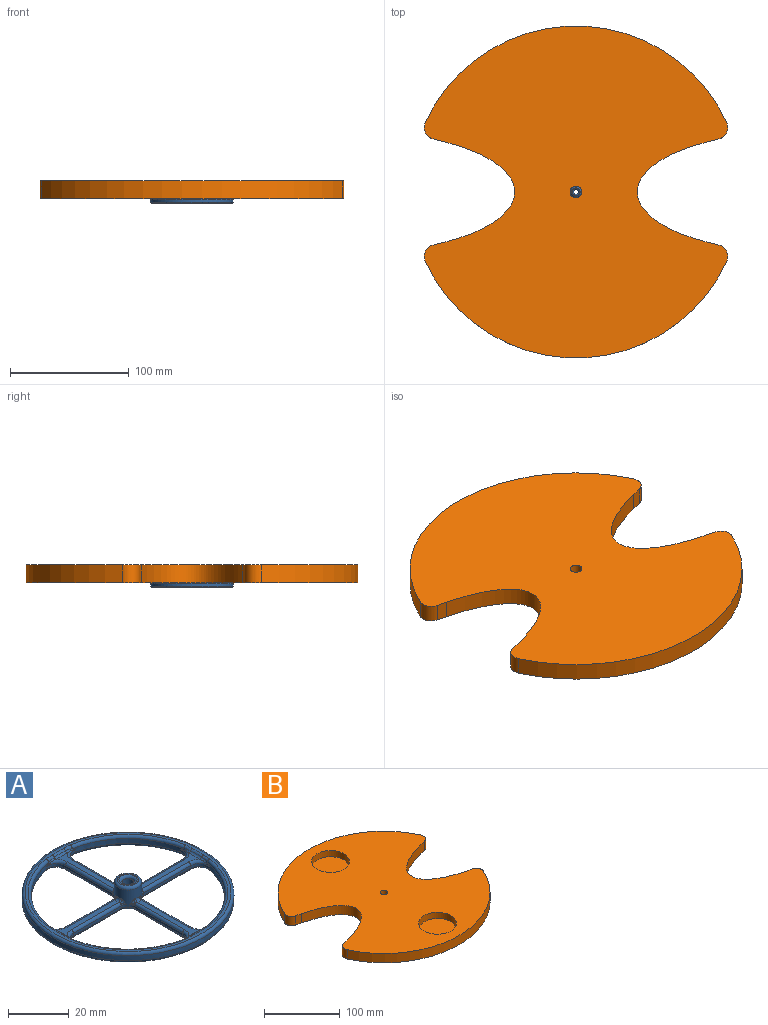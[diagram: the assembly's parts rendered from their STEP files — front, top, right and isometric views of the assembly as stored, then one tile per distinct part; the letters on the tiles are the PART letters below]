
ASSEMBLY  parts=2 mates=1
PART A: 147 faces, bbox 75.8x75.8x9 mm
  f0: cylinder r=32mm len=26.05mm, axis (0,0,1), area 74.3mm2, adj f24,f25,f54,f70,f98,f127
  f1: cylinder r=32mm len=26.05mm, axis (0,0,1), area 74.3mm2, adj f28,f29,f46,f59,f97,f111
  f2: cylinder r=32mm len=26.05mm, axis (0,0,1), area 74.3mm2, adj f26,f27,f74,f87,f106,f119
  f3: plane 68x68mm, normal (0,0,-1), area 521mm2, adj f110,f111,f112,f113,f114,f115,f116,f117
  f4: plane 68x68mm, normal (0,0,1), area 219.2mm2, adj f94,f95,f96,f97,f98,f99,f100,f101
  f5: cylinder r=2mm len=7mm, axis (0,0,-1), area 88mm2, adj f142,f146
  f6: cylinder r=35mm len=70mm, axis (0,0,-1), area 439.8mm2, adj f143,f144
  f7: cylinder r=4.5mm len=9mm, axis (0,0,-1), area 138.5mm2, adj f30,f31,f32,f33,f34,f35,f36,f37
  f8: plane 7x7mm, normal (0,0,1), area 10.2mm2, adj f145,f146
  f9: plane 22.23x1mm, normal (0,-1,0), area 22.2mm2, adj f29,f36,f63,f112
  f10: plane 22.23x1mm, normal (-1,0,0), area 22.2mm2, adj f28,f37,f50,f115
  f11: plane 22.23x1mm, normal (0,1,0), area 22.2mm2, adj f26,f34,f91,f120
  f12: plane 22.23x1mm, normal (1,0,0), area 22.2mm2, adj f27,f35,f78,f123
  f13: plane 22.23x1mm, normal (0,1,0), area 22.2mm2, adj f24,f33,f55,f131
  f14: plane 22.23x1mm, normal (-1,0,0), area 22.2mm2, adj f25,f32,f69,f128
  f15: plane 22.23x1mm, normal (0,-1,0), area 22.2mm2, adj f22,f31,f83,f139
  f16: plane 22.23x1mm, normal (1,0,0), area 22.2mm2, adj f23,f30,f41,f136
  f17: cylinder r=32mm len=26.05mm, axis (0,0,1), area 74.3mm2, adj f22,f23,f42,f82,f105,f135
  f18: plane 25.59x4.96mm, normal (0,0,1), area 54.5mm2, adj f39,f41,f44,f45,f48,f50
  f19: plane 25.59x4.96mm, normal (0,0,1), area 54.5mm2, adj f80,f83,f85,f88,f89,f91
  f20: plane 25.59x4.96mm, normal (0,0,1), area 54.5mm2, adj f67,f69,f72,f73,f76,f78
  f21: plane 25.59x4.96mm, normal (0,0,1), area 54.5mm2, adj f52,f55,f57,f60,f61,f63
  f22: cylinder r=4mm len=4.86mm, axis (0,0,1), area 7.1mm2, adj f15,f17,f80,f137
  f23: cylinder r=4mm len=4.86mm, axis (0,0,1), area 7.1mm2, adj f16,f17,f39,f134
  f24: cylinder r=4mm len=4.86mm, axis (0,0,1), area 7.1mm2, adj f0,f13,f52,f129
  f25: cylinder r=4mm len=4.86mm, axis (0,0,1), area 7.1mm2, adj f0,f14,f67,f126
  f26: cylinder r=4mm len=4.86mm, axis (0,0,1), area 7.1mm2, adj f2,f11,f89,f118
  f27: cylinder r=4mm len=4.86mm, axis (0,0,1), area 7.1mm2, adj f2,f12,f76,f121
  f28: cylinder r=4mm len=4.86mm, axis (0,0,1), area 7.1mm2, adj f1,f10,f48,f113
  f29: cylinder r=4mm len=4.86mm, axis (0,0,1), area 7.1mm2, adj f1,f9,f61,f110
  f30: cylinder r=2mm len=1.58mm, axis (0,0,-1), area 1.8mm2, adj f7,f16,f38,f138
  f31: cylinder r=2mm len=1.58mm, axis (0,0,-1), area 1.8mm2, adj f7,f15,f81,f141
  f32: cylinder r=2mm len=1.58mm, axis (0,0,-1), area 1.8mm2, adj f7,f14,f66,f130
  f33: cylinder r=2mm len=1.58mm, axis (0,0,-1), area 1.8mm2, adj f7,f13,f53,f133
  f34: cylinder r=2mm len=1.58mm, axis (0,0,-1), area 1.8mm2, adj f7,f11,f93,f122
  f35: cylinder r=2mm len=1.58mm, axis (0,0,-1), area 1.8mm2, adj f7,f12,f79,f125
  f36: cylinder r=2mm len=1.58mm, axis (0,0,-1), area 1.8mm2, adj f7,f9,f65,f114
  f37: cylinder r=2mm len=1.58mm, axis (0,0,-1), area 1.8mm2, adj f7,f10,f51,f117
  f38: torus R=3mm, axis (0,0,1), area 1mm2, adj f30,f40,f41
  f39: torus R=5mm, axis (0,0,1), area 8.7mm2, adj f18,f23,f41,f42
  f40: bspline ~1.86x1.69mm, area 1mm2, adj f7,f38,f43
  f41: cylinder r=1mm len=22.23mm, axis (0,1,0), area 34.8mm2, adj f16,f18,f38,f39,f43
  f42: bspline ~4.38x2mm, area 2.9mm2, adj f17,f39,f44,f103
  f43: bspline ~1.47x1.41mm, area 1mm2, adj f7,f40,f41,f45
  f44: torus R=31mm, axis (0,0,1), area 5.3mm2, adj f18,f42,f46,f101
  f45: torus R=5.5mm, axis (0,0,1), area 2.8mm2, adj f7,f18,f43,f47
  f46: bspline ~4.38x2mm, area 2.9mm2, adj f1,f44,f48,f99
  f47: bspline ~1.47x1.41mm, area 1mm2, adj f7,f45,f49,f50
  f48: torus R=5mm, axis (0,0,1), area 8.7mm2, adj f18,f28,f46,f50
  f49: bspline ~1.88x1.71mm, area 1mm2, adj f7,f47,f51
  f50: cylinder r=1mm len=22.23mm, axis (0,-1,0), area 34.8mm2, adj f10,f18,f47,f48,f51
  f51: torus R=3mm, axis (0,0,1), area 1mm2, adj f37,f49,f50
  f52: torus R=5mm, axis (0,0,1), area 8.7mm2, adj f21,f24,f54,f55
  f53: torus R=3mm, axis (0,0,1), area 1mm2, adj f33,f55,f56
  f54: bspline ~4.5x2mm, area 2.9mm2, adj f0,f52,f57,f96
  f55: cylinder r=1mm len=22.23mm, axis (-1,0,0), area 34.8mm2, adj f13,f21,f52,f53,f58
  f56: bspline ~1.88x1.71mm, area 1mm2, adj f7,f53,f58
  f57: torus R=31mm, axis (0,0,1), area 5.3mm2, adj f21,f54,f59,f94
  f58: bspline ~1.47x1.41mm, area 1mm2, adj f7,f55,f56,f60
  f59: bspline ~4.99x2mm, area 2.9mm2, adj f1,f57,f61,f95
  f60: torus R=5.5mm, axis (0,0,1), area 2.8mm2, adj f7,f21,f58,f62
  f61: torus R=5mm, axis (0,0,1), area 8.7mm2, adj f21,f29,f59,f63
  f62: bspline ~1.47x1.41mm, area 1mm2, adj f7,f60,f63,f64
  f63: cylinder r=1mm len=22.23mm, axis (1,0,0), area 34.8mm2, adj f9,f21,f61,f62,f65
  f64: bspline ~1.86x1.69mm, area 1mm2, adj f7,f62,f65
  f65: torus R=3mm, axis (0,0,1), area 1mm2, adj f36,f63,f64
  f66: torus R=3mm, axis (0,0,1), area 1mm2, adj f32,f68,f69
  f67: torus R=5mm, axis (0,0,1), area 8.7mm2, adj f20,f25,f69,f70
  f68: bspline ~1.86x1.69mm, area 1mm2, adj f7,f66,f71
  f69: cylinder r=1mm len=22.23mm, axis (0,-1,0), area 34.8mm2, adj f14,f20,f66,f67,f71
  f70: bspline ~4.38x2mm, area 2.9mm2, adj f0,f67,f72,f100
  f71: bspline ~1.47x1.41mm, area 1mm2, adj f7,f68,f69,f73
  f72: torus R=31mm, axis (0,0,1), area 5.3mm2, adj f20,f70,f74,f102
  f73: torus R=5.5mm, axis (0,0,1), area 2.8mm2, adj f7,f20,f71,f75
  f74: bspline ~4.38x2mm, area 2.9mm2, adj f2,f72,f76,f104
  f75: bspline ~1.47x1.41mm, area 1mm2, adj f7,f73,f77,f78
  f76: torus R=5mm, axis (0,0,1), area 8.7mm2, adj f20,f27,f74,f78
  f77: bspline ~1.88x1.71mm, area 1mm2, adj f7,f75,f79
  f78: cylinder r=1mm len=22.23mm, axis (0,1,0), area 34.8mm2, adj f12,f20,f75,f76,f79
  f79: torus R=3mm, axis (0,0,1), area 1mm2, adj f35,f77,f78
  f80: torus R=5mm, axis (0,0,1), area 8.7mm2, adj f19,f22,f82,f83
  f81: torus R=3mm, axis (0,0,1), area 1mm2, adj f31,f83,f84
  f82: bspline ~4.5x2mm, area 2.9mm2, adj f17,f80,f85,f107
  f83: cylinder r=1mm len=22.23mm, axis (1,0,0), area 34.8mm2, adj f15,f19,f80,f81,f86
  f84: bspline ~1.88x1.71mm, area 1mm2, adj f7,f81,f86
  f85: torus R=31mm, axis (0,0,1), area 5.3mm2, adj f19,f82,f87,f109
  f86: bspline ~1.47x1.41mm, area 1mm2, adj f7,f83,f84,f88
  f87: bspline ~4.99x2mm, area 2.9mm2, adj f2,f85,f89,f108
  f88: torus R=5.5mm, axis (0,0,1), area 2.8mm2, adj f7,f19,f86,f90
  f89: torus R=5mm, axis (0,0,1), area 8.7mm2, adj f19,f26,f87,f91
  f90: bspline ~1.47x1.41mm, area 1mm2, adj f7,f88,f91,f92
  f91: cylinder r=1mm len=22.23mm, axis (-1,0,0), area 34.8mm2, adj f11,f19,f89,f90,f93
  f92: bspline ~1.86x1.69mm, area 1mm2, adj f7,f90,f93
  f93: torus R=3mm, axis (0,0,1), area 1mm2, adj f34,f91,f92
  f94: torus R=32.73mm, axis (0,0,-1), area 5.4mm2, adj f4,f57,f95,f96
  f95: bspline ~4.35x1.63mm, area 3.7mm2, adj f4,f59,f94,f97
  f96: bspline ~3.52x1.15mm, area 3.7mm2, adj f4,f54,f94,f98
  f97: torus R=33mm, axis (0,0,-1), area 62.4mm2, adj f1,f4,f95,f99
  f98: torus R=33mm, axis (0,0,-1), area 62.4mm2, adj f0,f4,f96,f100
  f99: bspline ~3.64x1.19mm, area 3.7mm2, adj f4,f46,f97,f101
  f100: bspline ~4.35x1.63mm, area 3.7mm2, adj f4,f70,f98,f102
  f101: torus R=32.73mm, axis (0,0,-1), area 5.4mm2, adj f4,f44,f99,f103
  f102: torus R=32.73mm, axis (0,0,-1), area 5.4mm2, adj f4,f72,f100,f104
  f103: bspline ~4.35x1.63mm, area 3.7mm2, adj f4,f42,f101,f105
  f104: bspline ~3.64x1.19mm, area 3.7mm2, adj f4,f74,f102,f106
  f105: torus R=33mm, axis (0,0,-1), area 62.4mm2, adj f4,f17,f103,f107
  f106: torus R=33mm, axis (0,0,-1), area 62.4mm2, adj f2,f4,f104,f108
  f107: bspline ~3.64x1.19mm, area 3.7mm2, adj f4,f82,f105,f109
  f108: bspline ~4.35x1.63mm, area 3.7mm2, adj f4,f87,f106,f109
  f109: torus R=32.73mm, axis (0,0,-1), area 5.4mm2, adj f4,f85,f107,f108
  f110: torus R=5mm, axis (0,0,1), area 12.2mm2, adj f3,f29,f111,f112
  f111: torus R=33mm, axis (0,0,1), area 57.9mm2, adj f1,f3,f110,f113
  f112: cylinder r=1mm len=22.23mm, axis (-1,0,0), area 34.9mm2, adj f3,f9,f110,f114
  f113: torus R=5mm, axis (0,0,1), area 12.2mm2, adj f3,f28,f111,f115
  f114: torus R=3mm, axis (0,0,1), area 3.4mm2, adj f3,f36,f112,f116
  f115: cylinder r=1mm len=22.23mm, axis (0,1,0), area 34.9mm2, adj f3,f10,f113,f117
  f116: torus R=3.5mm, axis (0,0,1), area 1.6mm2, adj f3,f7,f114,f117
  f117: torus R=3mm, axis (0,0,1), area 3.4mm2, adj f3,f37,f115,f116
  f118: torus R=5mm, axis (0,0,1), area 12.2mm2, adj f3,f26,f119,f120
  f119: torus R=33mm, axis (0,0,1), area 57.9mm2, adj f2,f3,f118,f121
  f120: cylinder r=1mm len=22.23mm, axis (1,0,0), area 34.9mm2, adj f3,f11,f118,f122
  f121: torus R=5mm, axis (0,0,1), area 12.2mm2, adj f3,f27,f119,f123
  f122: torus R=3mm, axis (0,0,1), area 3.4mm2, adj f3,f34,f120,f124
  f123: cylinder r=1mm len=22.23mm, axis (0,-1,0), area 34.9mm2, adj f3,f12,f121,f125
  f124: torus R=3.5mm, axis (0,0,1), area 1.6mm2, adj f3,f7,f122,f125
  f125: torus R=3mm, axis (0,0,1), area 3.4mm2, adj f3,f35,f123,f124
  f126: torus R=5mm, axis (0,0,1), area 12.2mm2, adj f3,f25,f127,f128
  f127: torus R=33mm, axis (0,0,1), area 57.9mm2, adj f0,f3,f126,f129
  f128: cylinder r=1mm len=22.23mm, axis (0,1,0), area 34.9mm2, adj f3,f14,f126,f130
  f129: torus R=5mm, axis (0,0,1), area 12.2mm2, adj f3,f24,f127,f131
  f130: torus R=3mm, axis (0,0,1), area 3.4mm2, adj f3,f32,f128,f132
  f131: cylinder r=1mm len=22.23mm, axis (1,0,0), area 34.9mm2, adj f3,f13,f129,f133
  f132: torus R=3.5mm, axis (0,0,1), area 1.6mm2, adj f3,f7,f130,f133
  f133: torus R=3mm, axis (0,0,1), area 3.4mm2, adj f3,f33,f131,f132
  f134: torus R=5mm, axis (0,0,1), area 12.2mm2, adj f3,f23,f135,f136
  f135: torus R=33mm, axis (0,0,1), area 57.9mm2, adj f3,f17,f134,f137
  f136: cylinder r=1mm len=22.23mm, axis (0,-1,0), area 34.9mm2, adj f3,f16,f134,f138
  f137: torus R=5mm, axis (0,0,1), area 12.2mm2, adj f3,f22,f135,f139
  f138: torus R=3mm, axis (0,0,1), area 3.4mm2, adj f3,f30,f136,f140
  f139: cylinder r=1mm len=22.23mm, axis (-1,0,0), area 34.9mm2, adj f3,f15,f137,f141
  f140: torus R=3.5mm, axis (0,0,1), area 1.6mm2, adj f3,f7,f138,f141
  f141: torus R=3mm, axis (0,0,1), area 3.4mm2, adj f3,f31,f139,f140
  f142: torus R=3mm, axis (0,0,1), area 23.3mm2, adj f3,f5
  f143: torus R=34mm, axis (0,0,1), area 341.8mm2, adj f3,f6
  f144: torus R=34mm, axis (0,0,-1), area 341.8mm2, adj f4,f6
  f145: torus R=3.5mm, axis (0,0,-1), area 40.8mm2, adj f7,f8
  f146: torus R=3mm, axis (0,0,-1), area 23.3mm2, adj f5,f8
PART B: 19 faces, bbox 256.1x280x15 mm
  f0: extruded ~85x59.78mm, area 2337.1mm2, adj f1,f5,f6,f7
  f1: plane 15x8.97mm, normal (-0.24,0.97,0), area 138.6mm2, adj f0,f6,f7,f8
  f2: cylinder r=140mm len=254.28mm, axis (0,0,-1), area 4783mm2, adj f6,f7,f8,f13
  f3: cylinder r=5mm len=15mm, axis (0,0,-1), area 471.2mm2, adj f6,f7
  f4: cylinder r=140mm len=254.28mm, axis (0,0,-1), area 4783mm2, adj f6,f7,f9,f14
  f5: plane 15x8.97mm, normal (-0.24,-0.97,0), area 138.6mm2, adj f0,f6,f7,f9
  f6: plane 280x256.12mm, normal (0,0,1), area 45580.9mm2, adj f0,f1,f2,f3,f4,f5,f8,f9
  f7: plane 280x256.12mm, normal (0,0,-1), area 49507.9mm2, adj f0,f1,f2,f3,f4,f5,f8,f9
  f8: cylinder r=10mm len=15mm, axis (0,0,-1), area 264mm2, adj f1,f2,f6,f7
  f9: cylinder r=10mm len=15mm, axis (0,0,-1), area 264mm2, adj f4,f5,f6,f7
  f10: extruded ~85x59.78mm, area 2337.1mm2, adj f6,f7,f11,f12
  f11: plane 15x8.97mm, normal (0.24,0.97,0), area 138.6mm2, adj f6,f7,f10,f13
  f12: plane 15x8.97mm, normal (0.24,-0.97,0), area 138.6mm2, adj f6,f7,f10,f14
  f13: cylinder r=10mm len=15mm, axis (0,0,-1), area 264mm2, adj f2,f6,f7,f11
  f14: cylinder r=10mm len=15mm, axis (0,0,-1), area 264mm2, adj f4,f6,f7,f12
  f15: cylinder r=25mm len=50mm, axis (0,0,1), area 1570.8mm2, adj f6,f16
  f16: plane 50x50mm, normal (0,0,1), area 1963.5mm2, adj f15
  f17: cylinder r=25mm len=50mm, axis (0,0,1), area 1570.8mm2, adj f6,f18
  f18: plane 50x50mm, normal (0,0,1), area 1963.5mm2, adj f17
PLACE A t=(-107.31,-60.06,-8.66)mm
PLACE B rot(axis=(1,0,0),180deg) t=(-107.31,-60.06,10.34)mm
MATE fastened B.f3 <-> A.f5  axis (0,0,1) through (-107.31,-60.06,10.34)mm
